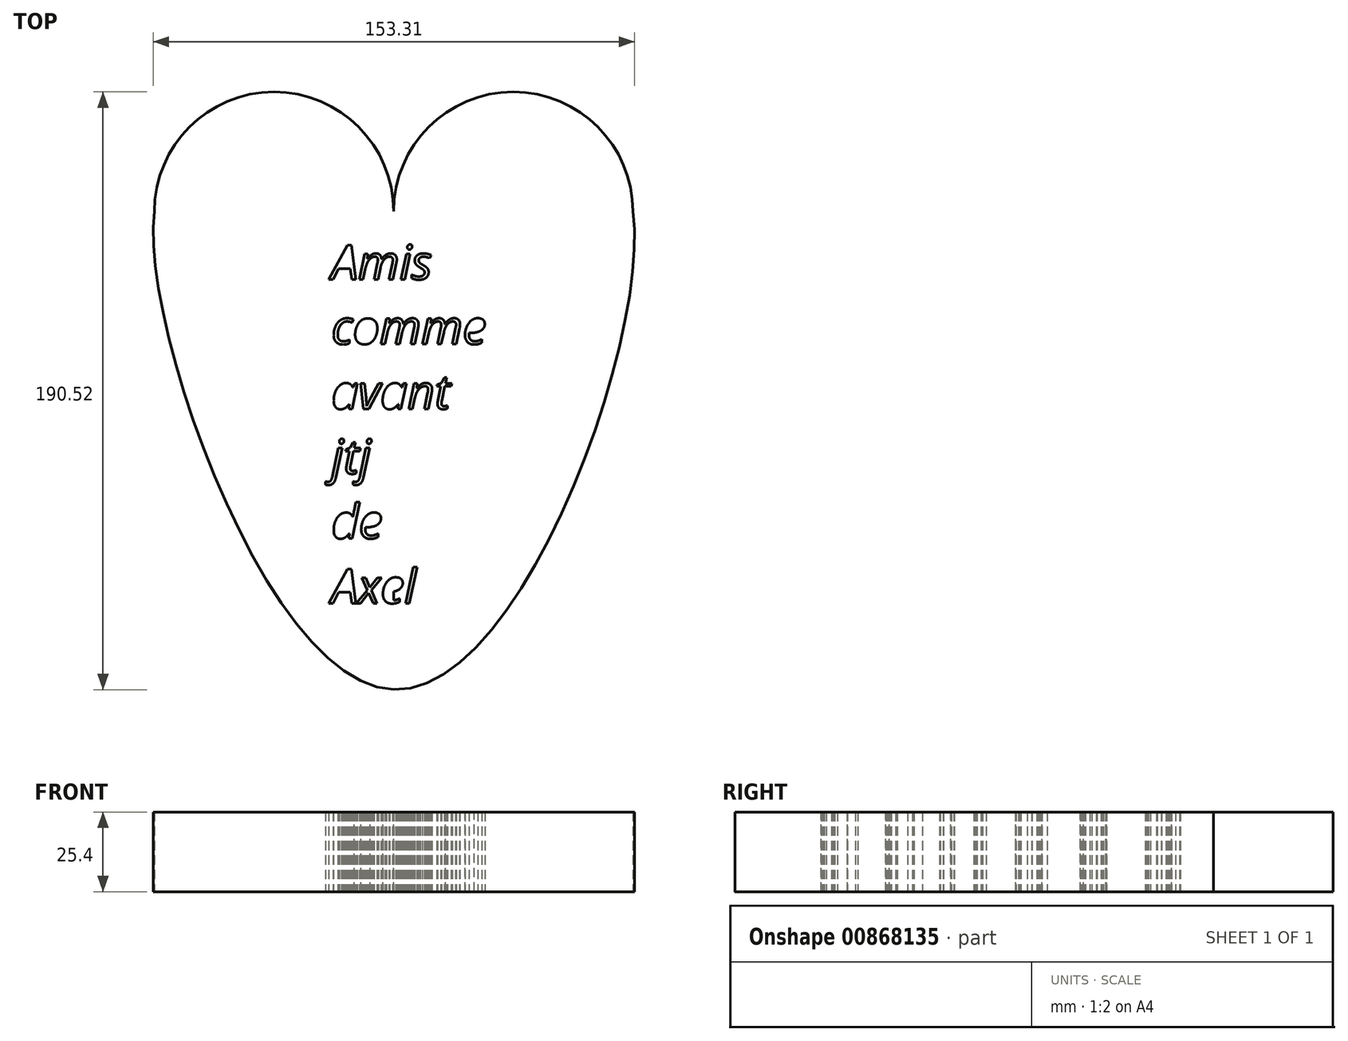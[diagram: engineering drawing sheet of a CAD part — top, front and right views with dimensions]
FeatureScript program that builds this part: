
annotation { "Feature Type Name" : "Feature", "Feature Type Description" : "" }
export const myFeature = defineFeature(function(context is Context, id is Id, definition is map)
    precondition{}
    {
        {
            var Q0;
            Q0=qCreatedBy(makeId("Top.planeOp"),FACE);
            var sketch = newSketch(context, id + "F0", { "sketchPlane" : qUnion([Q0])});
            skLineSegment(sketch, "E0", {"start": v(-74.5, 10.7) * mm, "end": v(77.9, 10.7) * mm});
            skPoint(sketch, "E1", {"position": v(1.7, 10.7) * mm});
            skPoint(sketch, "E2", {"position": v(-36.4, 10.7) * mm});
            skPoint(sketch, "E3", {"position": v(39.8, 10.7) * mm});
            skArc(sketch, "E4", {"start": v(1.7, 10.7) * mm, "mid": v(-36.4, 48.8) * mm, "end": v(-74.5, 10.7) * mm});
            skArc(sketch, "E5", {"start": v(77.9, 10.7) * mm, "mid": v(39.8, 48.8) * mm, "end": v(1.7, 10.7) * mm});
            skLineSegment(sketch, "E6", {"start": v(1.7, 10.7) * mm, "end": v(1.7, -141.7) * mm});
            skFitSpline(sketch, "E7", {"points": [v(-74.5, 10.7) * mm, v(1.7, -141.7) * mm, v(77.9, 10.7) * mm], "startDerivative": vector(-29.1, -209.12) * mm, "endDerivative": vector(-33.51, 242.87) * mm});
            skText(sketch, "E8", { "text": "Amis\ncomme\navant\njtj\nde\nAxel", "fontName": "OpenSans-Italic.ttf"});
            const initialGuessF0  = {"E8": [-0.01814, -0.01093, 1, 0, 0.01093]};
            skSetInitialGuess(sketch, initialGuessF0);
            skSolve(sketch);
        }
        {
            var Q0;
            Q0=qSketchRegion(id+"F0",true);
            extrude(context, id + "F1", {"entities" : qUnion([Q0]), "depth" : 25.4 * mm, "offsetDistance" : 25.4 * mm});
        }
    });
